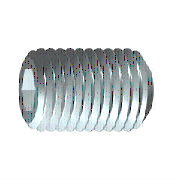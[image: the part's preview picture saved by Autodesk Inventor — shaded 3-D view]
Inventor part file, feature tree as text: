
AUTODESK INVENTOR PART (.ipt)
format: ipt  version: 2014 (Build 180170000, 170)  size: 168,448 bytes
history: native  units: mm (DEFAULTED — no unit token found)
features: sketch x2, extrude x1, other x1, plane x1
ambient origin geometry x8: Origin, YZ Plane, XZ Plane, XY Plane, X Axis, Y Axis, Z Axis, Center Point
bodies: Solid1 (feature_tree), Body (feature_tree)
feature tree (5):
  extrude  "Slot"  TaperAngle=60.0deg  [1 undecoded]
  other  "Work Axis1"
  plane  "Work Plane1"
  sketch  "Sketch1"  dims[d0=1.4mm d1=60.0deg]
  sketch  "Sketch2"  dims[d2=1.4mm d3=0.80829mm d6=90.0deg d4=3.0mm d5=60.0deg d7=0.7mm d8=1.4mm d9=0.0mm d10=0.35mm d11=45.0deg d12=0.184035mm d13=45.0deg d14=3.0mm d15=0.0mm d16=0.0mm d33=0.35mm d34=0.184035mm d35=0.0mm d37=0.0mm]
note: 1 required parameter value undecoded (feature->parameter linkage not recoverable at this tier; creation-order binding heuristic only, values carry confidence <= 0.55)
